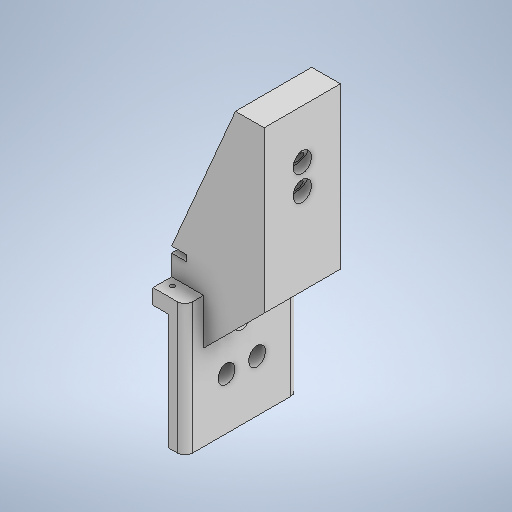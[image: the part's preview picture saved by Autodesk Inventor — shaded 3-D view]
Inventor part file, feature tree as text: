
AUTODESK INVENTOR PART (.ipt)
format: ipt  version: 2025.2 (Build 292293000, 293)  size: 430,080 bytes
history: native  units: in
note: dims shown in document units (in); Inventor stores cm internally (conversion verified against a paired STEP export)
features: extrude x17, sketch x13, plane x6, chamfer x2, fillet x1, projected_geometry x1
ambient origin geometry x8: Origin, YZ Plane, XZ Plane, XY Plane, X Axis, Y Axis, Z Axis, Center Point
bodies: Solid1 (feature_tree)
feature tree (40):
  sketch  "Sketch1"  dims[d0=0.4331in d1=2.9331in]
  extrude  "Extrusion1"  Depth=2.9331in
  extrude  "Extrusion2"  Depth=0.2854in
  extrude  "Extrusion3"  Depth=0.3937in TaperAngle=0.0deg
  plane  "Work Plane1"
  plane  "Work Plane3"
  sketch  "Sketch4"  dims[d9=0.4213in d10=2.9921in d11=0.0in]
  extrude  "Extrusion4"  Depth=2.9921in TaperAngle=0.0deg
  extrude  "Extrusion11"  Depth=0.1575in
  extrude  "Extrusion6"  Depth=0.1575in
  extrude  "Extrusion7"  Depth=0.3937in
  extrude  "Extrusion8"  Depth=0.5906in
  chamfer  "Chamfer1"  [1 undecoded]
  chamfer  "Chamfer2"  Distance=4.9213in
  extrude  "Extrusion12"  Depth=0.0787in
  plane  "Work Plane4"
  plane  "Work Plane5"
  plane  "Work Plane6"
  extrude  "Extrusion15"  Depth=0.1969in
  fillet  "Fillet1"  Radius=1.0207in
  extrude  "Extrusion16"  Depth=1.9685in TaperAngle=0.0deg
  extrude  "Extrusion18"  TaperAngle=0.0deg  [1 undecoded]
  extrude  "Extrusion19"  TaperAngle=90.0deg  [1 undecoded]
  extrude  "Extrusion20"  Depth=0.3937in
  extrude  "Extrusion22"  Depth=0.1575in
  plane  "Work Plane8"
  sketch  "Sketch19"  dims[d62=-1.378in d68=0.0in d69=90.0deg d76=0.3937in d77=0.1575in d78=2.7756in d79=0.0in d80=0.1969in d81=0.2362in d82=0.2362in d83=0.3937in d84=0.3543in d85=0.0in d88=0.2756in d89=0.0in d91=135.0deg d92=1.9685in d93=0.0in d94=0.3543in d95=0.0in d99=0.4724in d100=0.748in d103=0.2756in d104=0.2756in d105=0.5906in d106=0.3937in d107=0.0in d108=-0.9843in d109=0.4724in d110=0.4724in d111=0.3937in d112=0.0in d113=0.6299in d114=0.0in]
  extrude  "Extrusion23"  Depth=0.3937in TaperAngle=0.0deg
  extrude  "Extrusion24"  Depth=0.1969in
  sketch  "Sketch2"  dims[d2=0.1181in d3=0.2854in]
  sketch  "Sketch3"  dims[d5=0.3937in d6=0.0in d7=0.3937in d8=0.0in]
  sketch  "Sketch5"  dims[d12=1.0668in d13=0.1575in]
  sketch  "Sketch8"  dims[d14=0.4331in d15=0.1575in d16=0.4331in]
  sketch  "Sketch11"  dims[d19=0.3937in d20=0.9331in]
  sketch  "Sketch12"  dims[d21=0.5906in d22=0.0in d23=2.1457in d26=0.0in d27=0.0in]
  sketch  "Sketch14"  dims[d28=1.9685in d29=4.9213in d30=0.0in]
  sketch  "Sketch15"  dims[d31=1.5748in d32=0.0in d33=1.5748in d34=0.0787in d35=0.1598in]
  projected_geometry  "Projected Loop1"
  sketch  "Sketch16"  dims[d51=1.1811in d52=1.1811in d53=0.7782in d56=0.1969in d57=1.0207in d58=0.0in]
  sketch  "Sketch18"  dims[d59=1.9685in d60=0.8937in d61=0.0in]
note: 3 required parameter values undecoded (feature->parameter linkage not recoverable at this tier; creation-order binding heuristic only, values carry confidence <= 0.55)
